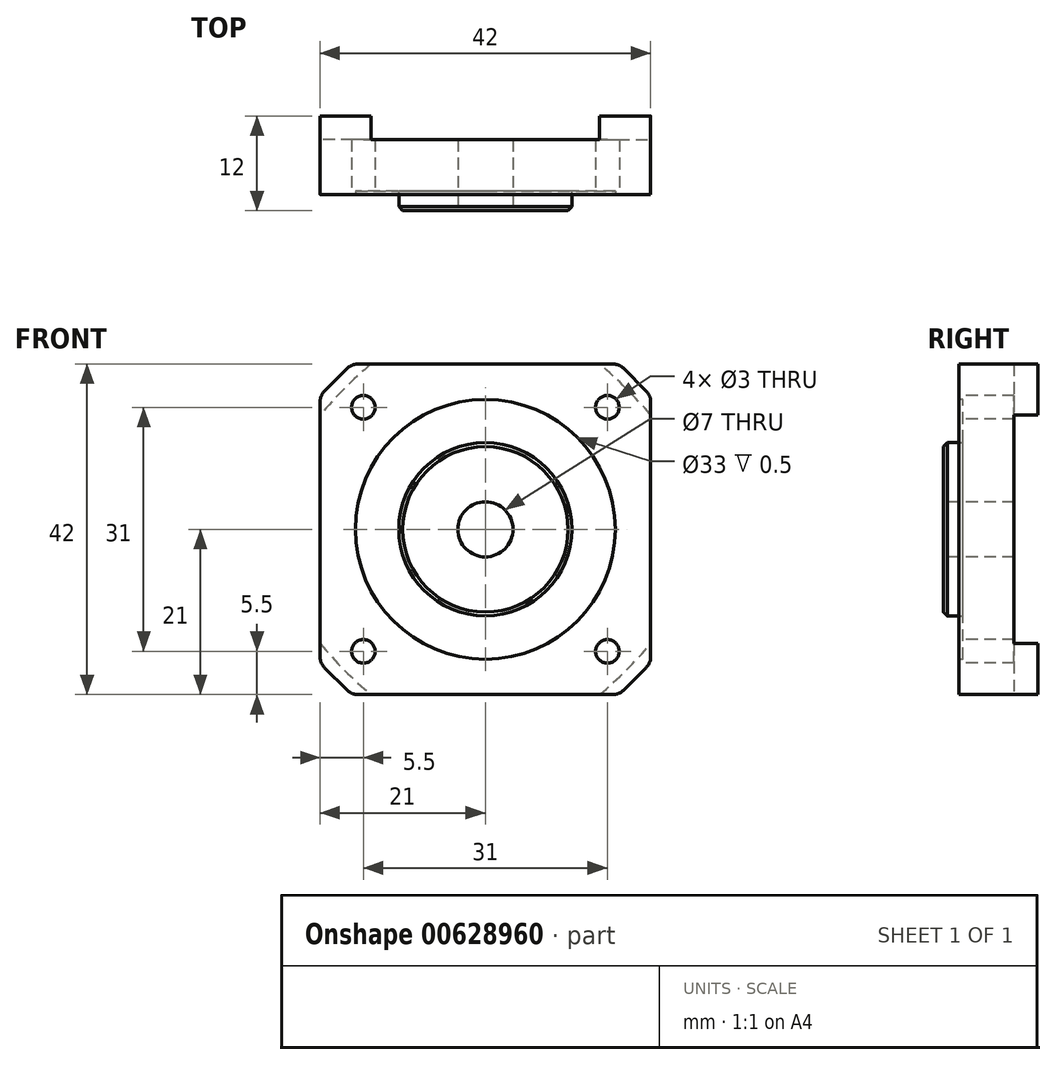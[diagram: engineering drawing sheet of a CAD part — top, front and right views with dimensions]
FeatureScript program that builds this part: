
annotation { "Feature Type Name" : "Feature", "Feature Type Description" : "" }
export const myFeature = defineFeature(function(context is Context, id is Id, definition is map)
    precondition{}
    {
        {
            var Q0;
            Q0=qCreatedBy(makeId("Front.planeOp"),FACE);
            var sketch = newSketch(context, id + "F0", { "sketchPlane" : qUnion([Q0])});
            skLineSegment(sketch, "E0.bottom", {"start": v(-21, 21) * mm, "end": v(21, 21) * mm});
            skLineSegment(sketch, "E0.top", {"start": v(-21, -21) * mm, "end": v(21, -21) * mm});
            skLineSegment(sketch, "E0.left", {"start": v(-21, 21) * mm, "end": v(-21, -21) * mm});
            skLineSegment(sketch, "E0.right", {"start": v(21, 21) * mm, "end": v(21, -21) * mm});
            skPoint(sketch, "E0.middle", {"position": v(0, 0) * mm});
            skSolve(sketch);
        }
        {
            var Q0;
            Q0=makeQuery(id+"F0.imprint","IMPRINT",FACE,{"disambiguationData":[TD([[makeQuery(id+"F0.imprint","IMPRINT",EDGE,{"derivedFrom":sQuery(id+"F0.wireOp",EDGE,"E0.bottom")}),-1.0]])]});
            extrude(context, id + "F1", {"entities" : qUnion([Q0]), "depth" : 10 * mm, "offsetDistance" : 25 * mm});
        }
        {
            var Q0;
            Q0=makeQuery(id+"F1.opExtrude","SWEPT_EDGE",EDGE,{"disambiguationData":[OSD([sQuery(id+"F0.wireOp",EDGE,"E0.bottom"),sQuery(id+"F0.wireOp",EDGE,"E0.left")])]});
            var Q1;
            Q1=makeQuery(id+"F1.opExtrude","SWEPT_EDGE",EDGE,{"disambiguationData":[OSD([sQuery(id+"F0.wireOp",EDGE,"E0.bottom"),sQuery(id+"F0.wireOp",EDGE,"E0.right")])]});
            var Q2;
            Q2=makeQuery(id+"F1.opExtrude","SWEPT_EDGE",EDGE,{"disambiguationData":[OSD([sQuery(id+"F0.wireOp",EDGE,"E0.top"),sQuery(id+"F0.wireOp",EDGE,"E0.right")])]});
            var Q3;
            Q3=makeQuery(id+"F1.opExtrude","SWEPT_EDGE",EDGE,{"disambiguationData":[OSD([sQuery(id+"F0.wireOp",EDGE,"E0.top"),sQuery(id+"F0.wireOp",EDGE,"E0.left")])]});
            chamfer(context, id + "F2", {"entities" : qUnion([Q0, Q1, Q2, Q3]), "width" : 4 * mm, "tangentPropagation" : true});
        }
        {
            var Q0;
            Q0=makeQuery(id+"F1.opExtrude","CAP_FACE",FACE,{"disambiguationData":[OSD([sQuery(id+"F0.wireOp",EDGE,"E0.bottom"),sQuery(id+"F0.wireOp",EDGE,"E0.top"),sQuery(id+"F0.wireOp",EDGE,"E0.left"),sQuery(id+"F0.wireOp",EDGE,"E0.right")])],"isStart":false});
            var sketch = newSketch(context, id + "F3", { "sketchPlane" : qUnion([Q0])});
            skCircle(sketch, "E1", {"center": v(0, 0) * mm, "radius": 16.5 * mm});
            skSolve(sketch);
        }
        {
            var Q0;
            Q0=makeQuery(id+"F3.imprint","IMPRINT",FACE,{"disambiguationData":[TD([[makeQuery(id+"F3.imprint","IMPRINT",EDGE,{"derivedFrom":sQuery(id+"F3.wireOp",EDGE,"E1")}),1.0]])]});
            extrude(context, id + "F4", {"entities" : qUnion([Q0]), "operationType" : NewBodyOperationType.REMOVE, "oppositeDirection" : true, "depth" : 0.5 * mm, "offsetDistance" : 25 * mm});
        }
        {
            var Q0;
            Q0=makeQuery(id+"F4.boolean.opBoolean","COPY",FACE,{"derivedFrom":makeQuery(id+"F4.opExtrude","CAP_FACE",FACE,{"disambiguationData":[OSD([sQuery(id+"F3.wireOp",EDGE,"E1")])],"isStart":false})});
            var sketch = newSketch(context, id + "F5", { "sketchPlane" : qUnion([Q0])});
            skCircle(sketch, "E2", {"center": v(0, 0) * mm, "radius": 11 * mm});
            skSolve(sketch);
        }
        {
            var Q0;
            Q0=makeQuery(id+"F5.imprint","IMPRINT",FACE,{"disambiguationData":[TD([[makeQuery(id+"F5.imprint","IMPRINT",EDGE,{"derivedFrom":sQuery(id+"F5.wireOp",EDGE,"E2")}),1.0]])]});
            extrude(context, id + "F6", {"entities" : qUnion([Q0]), "operationType" : NewBodyOperationType.ADD, "depth" : 2.5 * mm, "offsetDistance" : 25 * mm});
        }
        {
            var Q0;
            Q0=makeQuery(id+"F6.opExtrude","CAP_FACE",FACE,{"disambiguationData":[OSD([sQuery(id+"F5.wireOp",EDGE,"E2")])],"isStart":false});
            var sketch = newSketch(context, id + "F7", { "sketchPlane" : qUnion([Q0])});
            skCircle(sketch, "E3", {"center": v(0, 0) * mm, "radius": 3.5 * mm});
            skSolve(sketch);
        }
        {
            var Q0;
            Q0=makeQuery(id+"F7.imprint","IMPRINT",FACE,{"disambiguationData":[TD([[makeQuery(id+"F7.imprint","IMPRINT",EDGE,{"derivedFrom":sQuery(id+"F7.wireOp",EDGE,"E3")}),1.0]])]});
            var Q1;
            Q1=sQuery(id+"F7.wireOp",EDGE,"E3");
            extrude(context, id + "F8", {"entities" : qUnion([Q0]), "operationType" : NewBodyOperationType.REMOVE, "surfaceEntities" : qUnion([Q1]), "endBound" : BoundingType.THROUGH_ALL, "oppositeDirection" : true, "depth" : 25 * mm, "offsetDistance" : 25 * mm});
        }
        {
            var Q0;
            {var subQ0=sQuery(id+"F0.wireOp",EDGE,"E0.bottom");Q0=makeQuery(id+"F2.opChamfer","BLEND_EDGE",EDGE,{"blendedFrom":[makeQuery(id+"F1.opExtrude","SWEPT_EDGE",EDGE,{"disambiguationData":[OSD([subQ0,sQuery(id+"F0.wireOp",EDGE,"E0.left")])]}),makeQuery(id+"F1.opExtrude","SWEPT_FACE",FACE,{"disambiguationData":[OSD([subQ0])]})],"blendedInto":[makeQuery(id+"F1.opExtrude","SWEPT_FACE",FACE,{"disambiguationData":[OSD([subQ0])]})]});}
            var Q1;
            {var subQ0=sQuery(id+"F0.wireOp",EDGE,"E0.bottom");Q1=makeQuery(id+"F2.opChamfer","BLEND_EDGE",EDGE,{"blendedFrom":[makeQuery(id+"F1.opExtrude","SWEPT_EDGE",EDGE,{"disambiguationData":[OSD([subQ0,sQuery(id+"F0.wireOp",EDGE,"E0.right")])]}),makeQuery(id+"F1.opExtrude","SWEPT_FACE",FACE,{"disambiguationData":[OSD([subQ0])]})],"blendedInto":[makeQuery(id+"F1.opExtrude","SWEPT_FACE",FACE,{"disambiguationData":[OSD([subQ0])]})]});}
            var Q2;
            {var subQ0=sQuery(id+"F0.wireOp",EDGE,"E0.right");Q2=makeQuery(id+"F2.opChamfer","BLEND_EDGE",EDGE,{"blendedFrom":[makeQuery(id+"F1.opExtrude","SWEPT_EDGE",EDGE,{"disambiguationData":[OSD([sQuery(id+"F0.wireOp",EDGE,"E0.bottom"),subQ0])]}),makeQuery(id+"F1.opExtrude","SWEPT_FACE",FACE,{"disambiguationData":[OSD([subQ0])]})],"blendedInto":[makeQuery(id+"F1.opExtrude","SWEPT_FACE",FACE,{"disambiguationData":[OSD([subQ0])]})]});}
            var Q3;
            {var subQ0=sQuery(id+"F0.wireOp",EDGE,"E0.right");Q3=makeQuery(id+"F2.opChamfer","BLEND_EDGE",EDGE,{"blendedFrom":[makeQuery(id+"F1.opExtrude","SWEPT_EDGE",EDGE,{"disambiguationData":[OSD([sQuery(id+"F0.wireOp",EDGE,"E0.top"),subQ0])]}),makeQuery(id+"F1.opExtrude","SWEPT_FACE",FACE,{"disambiguationData":[OSD([subQ0])]})],"blendedInto":[makeQuery(id+"F1.opExtrude","SWEPT_FACE",FACE,{"disambiguationData":[OSD([subQ0])]})]});}
            var Q4;
            {var subQ0=sQuery(id+"F0.wireOp",EDGE,"E0.top");Q4=makeQuery(id+"F2.opChamfer","BLEND_EDGE",EDGE,{"blendedFrom":[makeQuery(id+"F1.opExtrude","SWEPT_EDGE",EDGE,{"disambiguationData":[OSD([subQ0,sQuery(id+"F0.wireOp",EDGE,"E0.right")])]}),makeQuery(id+"F1.opExtrude","SWEPT_FACE",FACE,{"disambiguationData":[OSD([subQ0])]})],"blendedInto":[makeQuery(id+"F1.opExtrude","SWEPT_FACE",FACE,{"disambiguationData":[OSD([subQ0])]})]});}
            var Q5;
            {var subQ0=sQuery(id+"F0.wireOp",EDGE,"E0.top");Q5=makeQuery(id+"F2.opChamfer","BLEND_EDGE",EDGE,{"blendedFrom":[makeQuery(id+"F1.opExtrude","SWEPT_EDGE",EDGE,{"disambiguationData":[OSD([subQ0,sQuery(id+"F0.wireOp",EDGE,"E0.left")])]}),makeQuery(id+"F1.opExtrude","SWEPT_FACE",FACE,{"disambiguationData":[OSD([subQ0])]})],"blendedInto":[makeQuery(id+"F1.opExtrude","SWEPT_FACE",FACE,{"disambiguationData":[OSD([subQ0])]})]});}
            var Q6;
            {var subQ0=sQuery(id+"F0.wireOp",EDGE,"E0.left");Q6=makeQuery(id+"F2.opChamfer","BLEND_EDGE",EDGE,{"blendedFrom":[makeQuery(id+"F1.opExtrude","SWEPT_EDGE",EDGE,{"disambiguationData":[OSD([sQuery(id+"F0.wireOp",EDGE,"E0.top"),subQ0])]}),makeQuery(id+"F1.opExtrude","SWEPT_FACE",FACE,{"disambiguationData":[OSD([subQ0])]})],"blendedInto":[makeQuery(id+"F1.opExtrude","SWEPT_FACE",FACE,{"disambiguationData":[OSD([subQ0])]})]});}
            var Q7;
            {var subQ0=sQuery(id+"F0.wireOp",EDGE,"E0.left");Q7=makeQuery(id+"F2.opChamfer","BLEND_EDGE",EDGE,{"blendedFrom":[makeQuery(id+"F1.opExtrude","SWEPT_EDGE",EDGE,{"disambiguationData":[OSD([sQuery(id+"F0.wireOp",EDGE,"E0.bottom"),subQ0])]}),makeQuery(id+"F1.opExtrude","SWEPT_FACE",FACE,{"disambiguationData":[OSD([subQ0])]})],"blendedInto":[makeQuery(id+"F1.opExtrude","SWEPT_FACE",FACE,{"disambiguationData":[OSD([subQ0])]})]});}
            fillet(context, id + "F9", {"entities" : qUnion([Q0, Q1, Q2, Q3, Q4, Q5, Q6, Q7]), "radius" : 2 * mm, "tangentPropagation" : true, "allowEdgeOverflow" : false});
        }
        {
            var Q0;
            Q0=makeQuery(id+"F6.opExtrude","CAP_EDGE",EDGE,{"disambiguationData":[OSD([sQuery(id+"F5.wireOp",EDGE,"E2")])],"isStart":false});
            var Q1;
            Q1=makeQuery(id+"F8.boolean.opBoolean","COPY",EDGE,{"derivedFrom":makeQuery(id+"F8.opExtrude","CAP_EDGE",EDGE,{"disambiguationData":[OSD([sQuery(id+"F7.wireOp",EDGE,"E3")])],"isStart":true})});
            var Q2;
            Q2=makeQuery(id+"F6.opExtrude","CAP_EDGE",EDGE,{"disambiguationData":[OSD([sQuery(id+"F5.wireOp",EDGE,"E2")])],"isStart":true});
            chamfer(context, id + "F10", {"entities" : qUnion([Q0, Q1, Q2]), "width" : 0.5 * mm, "tangentPropagation" : true});
        }
        {
            var Q0;
            Q0=makeQuery(id+"F1.opExtrude","CAP_FACE",FACE,{"disambiguationData":[OSD([sQuery(id+"F0.wireOp",EDGE,"E0.bottom"),sQuery(id+"F0.wireOp",EDGE,"E0.top"),sQuery(id+"F0.wireOp",EDGE,"E0.left"),sQuery(id+"F0.wireOp",EDGE,"E0.right")])],"isStart":true});
            var sketch = newSketch(context, id + "F11", { "sketchPlane" : qUnion([Q0])});
            skLineSegment(sketch, "E4.bottom", {"start": v(-21, 21) * mm, "end": v(21, 21) * mm, "construction": true});
            skLineSegment(sketch, "E4.top", {"start": v(-21, -21) * mm, "end": v(21, -21) * mm, "construction": true});
            skLineSegment(sketch, "E4.left", {"start": v(-21, 21) * mm, "end": v(-21, -21) * mm, "construction": true});
            skLineSegment(sketch, "E4.right", {"start": v(21, 21) * mm, "end": v(21, -21) * mm, "construction": true});
            skPoint(sketch, "E4.middle", {"position": v(0, 0) * mm});
            skArc(sketch, "E5", {"start": v(-21, 14.51) * mm, "mid": v(-17.9, 17.9) * mm, "end": v(-14.51, 21) * mm});
            skArc(sketch, "E6.1.0", {"start": v(-14.51, -21) * mm, "mid": v(-17.9, -17.9) * mm, "end": v(-21, -14.51) * mm});
            skArc(sketch, "E6.2.0", {"start": v(21, -14.51) * mm, "mid": v(17.9, -17.9) * mm, "end": v(14.51, -21) * mm});
            skArc(sketch, "E6.3.0", {"start": v(14.51, 21) * mm, "mid": v(17.9, 17.9) * mm, "end": v(21, 14.51) * mm});
            skLineSegment(sketch, "E7", {"start": v(-21, 14.51) * mm, "end": v(-21, -14.51) * mm});
            skLineSegment(sketch, "E8", {"start": v(-14.51, -21) * mm, "end": v(14.51, -21) * mm});
            skLineSegment(sketch, "E9", {"start": v(21, -14.51) * mm, "end": v(21, 14.51) * mm});
            skLineSegment(sketch, "E10", {"start": v(14.51, 21) * mm, "end": v(-14.51, 21) * mm});
            skSolve(sketch);
        }
        {
            var Q0;
            Q0=qSketchRegion(id+"F11",true);
            extrude(context, id + "F12", {"entities" : qUnion([Q0]), "operationType" : NewBodyOperationType.REMOVE, "oppositeDirection" : true, "depth" : 3 * mm, "offsetDistance" : 25 * mm});
        }
        {
            var Q0;
            Q0=makeQuery(id+"F1.opExtrude","CAP_FACE",FACE,{"disambiguationData":[OSD([sQuery(id+"F0.wireOp",EDGE,"E0.bottom"),sQuery(id+"F0.wireOp",EDGE,"E0.top"),sQuery(id+"F0.wireOp",EDGE,"E0.left"),sQuery(id+"F0.wireOp",EDGE,"E0.right")])],"isStart":false});
            var sketch = newSketch(context, id + "F13", { "sketchPlane" : qUnion([Q0])});
            skCircle(sketch, "E11", {"center": v(-15.5, 15.5) * mm, "radius": 1.5 * mm});
            skCircle(sketch, "E12.1.0", {"center": v(-15.5, -15.5) * mm, "radius": 1.5 * mm});
            skCircle(sketch, "E12.2.0", {"center": v(15.5, -15.5) * mm, "radius": 1.5 * mm});
            skCircle(sketch, "E12.3.0", {"center": v(15.5, 15.5) * mm, "radius": 1.5 * mm});
            skPoint(sketch, "E12.center", {"position": v(0, 0) * mm});
            skSolve(sketch);
        }
        {
            var Q0;
            Q0=qSketchRegion(id+"F13",true);
            extrude(context, id + "F14", {"entities" : qUnion([Q0]), "operationType" : NewBodyOperationType.REMOVE, "endBound" : BoundingType.THROUGH_ALL, "oppositeDirection" : true, "depth" : 25 * mm, "offsetDistance" : 25 * mm});
        }
    });
